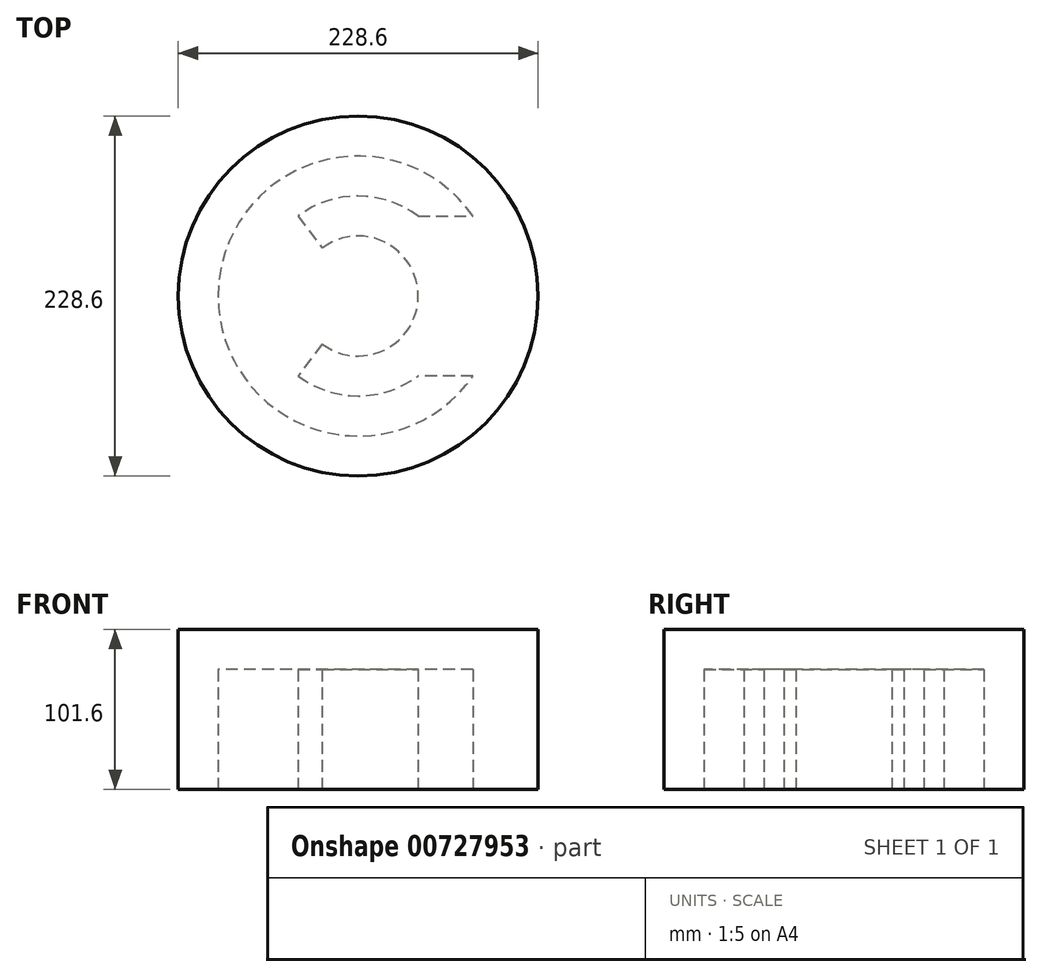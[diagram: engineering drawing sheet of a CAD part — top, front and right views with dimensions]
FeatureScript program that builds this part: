
annotation { "Feature Type Name" : "Feature", "Feature Type Description" : "" }
export const myFeature = defineFeature(function(context is Context, id is Id, definition is map)
    precondition{}
    {
        {
            var Q0;
            Q0=qCreatedBy(makeId("Top.planeOp"),FACE);
            var sketch = newSketch(context, id + "F0", { "sketchPlane" : qUnion([Q0])});
            skCircle(sketch, "E0", {"center": v(0, 0) * mm, "radius": 114.3 * mm});
            skCircle(sketch, "E1", {"center": v(0, 0) * mm, "radius": 38.1 * mm});
            skCircle(sketch, "E2", {"center": v(0, 0) * mm, "radius": 63.5 * mm});
            skCircle(sketch, "E3", {"center": v(0, 0) * mm, "radius": 88.9 * mm});
            skLineSegment(sketch, "E4", {"start": v(38.1, 50.8) * mm, "end": v(72.96, 50.8) * mm});
            skLineSegment(sketch, "E5", {"start": v(72.96, -50.8) * mm, "end": v(38.1, -50.8) * mm});
            skArc(sketch, "E6", {"start": v(72.96, -50.8) * mm, "mid": v(88.9, 0) * mm, "end": v(72.96, 50.8) * mm});
            skLineSegment(sketch, "E7", {"start": v(-38.1, 50.8) * mm, "end": v(-22.9, 30.45) * mm});
            skLineSegment(sketch, "E8", {"start": v(-22.9, -30.45) * mm, "end": v(-38.1, -50.8) * mm});
            skSolve(sketch);
        }
        {
            var Q0;
            Q0=qCreatedBy(makeId("Top.planeOp"),FACE);
            var sketch = newSketch(context, id + "F1", { "sketchPlane" : qUnion([Q0])});
            skSolve(sketch);
        }
        {
            var Q0;
            {var subQ4=sQuery(id+"F0.wireOp",EDGE,"E7");Q0=makeQuery(id+"F0.imprint","IMPRINT",FACE,{"disambiguationData":[TD([[makeQuery(id+"F0.imprint","IMPRINT",EDGE,{"derivedFrom":subQ4}),1.0]])]});}
            var Q1;
            {var subQ0=sQuery(id+"F0.wireOp",EDGE,"E4");Q1=makeQuery(id+"F0.imprint","IMPRINT",FACE,{"disambiguationData":[TD([[makeQuery(id+"F0.imprint","IMPRINT",EDGE,{"derivedFrom":subQ0}),-1.0]])]});}
            var Q2;
            Q2=makeQuery(id+"F0.imprint","IMPRINT",FACE,{"disambiguationData":[TD([[makeQuery(id+"F0.imprint","IMPRINT",EDGE,{"derivedFrom":sQuery(id+"F0.wireOp",EDGE,"E0")}),1.0]])]});
            extrude(context, id + "F2", {"entities" : qUnion([Q0, Q1, Q2]), "depth" : 101.6 * mm, "offsetDistance" : 25.4 * mm});
        }
        {
            var Q0;
            Q0=makeQuery(id+"F2.opExtrude","CAP_FACE",FACE,{"disambiguationData":[OSD([sQuery(id+"F0.wireOp",EDGE,"E0"),sQuery(id+"F0.wireOp",EDGE,"E1"),sQuery(id+"F0.wireOp",EDGE,"E2"),sQuery(id+"F0.wireOp",EDGE,"E3"),sQuery(id+"F0.wireOp",EDGE,"E4"),sQuery(id+"F0.wireOp",EDGE,"E5"),sQuery(id+"F0.wireOp",EDGE,"E7"),sQuery(id+"F0.wireOp",EDGE,"E8")])],"isStart":false});
            var sketch = newSketch(context, id + "F3", { "sketchPlane" : qUnion([Q0])});
            skSolve(sketch);
        }
        {
            var Q0;
            Q0 = qSketchRegion(id + "F1", true);
            var Q1;
            Q1=makeQuery(id+"F3.imprint","IMPRINT",FACE,{"disambiguationData":[TD([[makeQuery(id+"F3.imprint","IMPRINT",EDGE,{"derivedFrom":makeQuery(id+"F2.opExtrude","CAP_EDGE",EDGE,{"disambiguationData":[OSD([sQuery(id+"F0.wireOp",EDGE,"E1")])],"isStart":false})}),1.0]])]});
            extrude(context, id + "F4", {"entities" : qUnion([Q0, Q1]), "operationType" : NewBodyOperationType.ADD, "oppositeDirection" : true, "depth" : 25.4 * mm, "offsetDistance" : 25.4 * mm});
        }
    });
